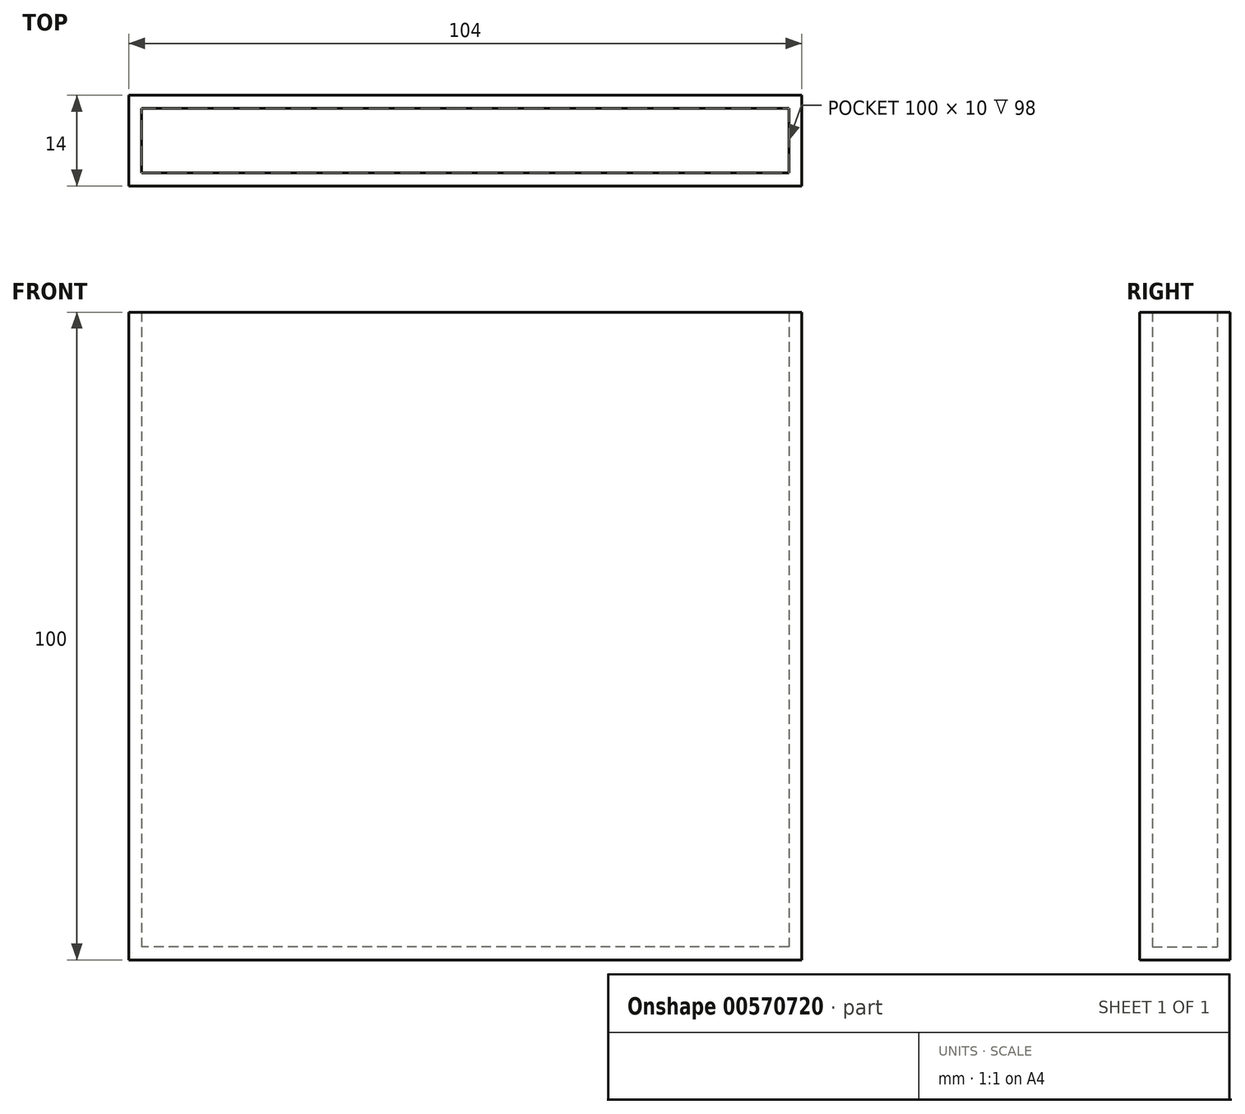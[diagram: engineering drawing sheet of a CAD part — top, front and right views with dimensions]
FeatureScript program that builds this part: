
annotation { "Feature Type Name" : "Feature", "Feature Type Description" : "" }
export const myFeature = defineFeature(function(context is Context, id is Id, definition is map)
    precondition{}
    {
        {
            var Q0;
            Q0=qCreatedBy(makeId("Top.planeOp"),FACE);
            var sketch = newSketch(context, id + "F0", { "sketchPlane" : qUnion([Q0])});
            skPoint(sketch, "E0.middle", {"position": v(0, 0) * mm});
            skLineSegment(sketch, "E1.bottom", {"start": v(52, -7) * mm, "end": v(-52, -7) * mm});
            skLineSegment(sketch, "E1.top", {"start": v(52, 7) * mm, "end": v(-52, 7) * mm});
            skLineSegment(sketch, "E1.left", {"start": v(52, -7) * mm, "end": v(52, 7) * mm});
            skLineSegment(sketch, "E1.right", {"start": v(-52, -7) * mm, "end": v(-52, 7) * mm});
            skLineSegment(sketch, "E2.bottom", {"start": v(-50, 5) * mm, "end": v(50, 5) * mm});
            skLineSegment(sketch, "E2.top", {"start": v(-50, -5) * mm, "end": v(50, -5) * mm});
            skLineSegment(sketch, "E2.left", {"start": v(-50, 5) * mm, "end": v(-50, -5) * mm});
            skLineSegment(sketch, "E2.right", {"start": v(50, 5) * mm, "end": v(50, -5) * mm});
            skSolve(sketch);
        }
        {
            var Q0;
            Q0=qSketchRegion(id+"F0",true);
            var Q1;
            Q1=makeQuery(id+"F0.imprint","IMPRINT",FACE,{"disambiguationData":[TD([[makeQuery(id+"F0.imprint","IMPRINT",EDGE,{"derivedFrom":sQuery(id+"F0.wireOp",EDGE,"E2.bottom")}),-1.0]])]});
            extrude(context, id + "F1", {"entities" : qUnion([Q0, Q1]), "depth" : 2 * mm, "offsetDistance" : 25 * mm});
        }
        {
            var Q0;
            Q0=qSketchRegion(id+"F0",true);
            extrude(context, id + "F2", {"entities" : qUnion([Q0]), "operationType" : NewBodyOperationType.ADD, "depth" : 100 * mm, "offsetDistance" : 25 * mm});
        }
    });
